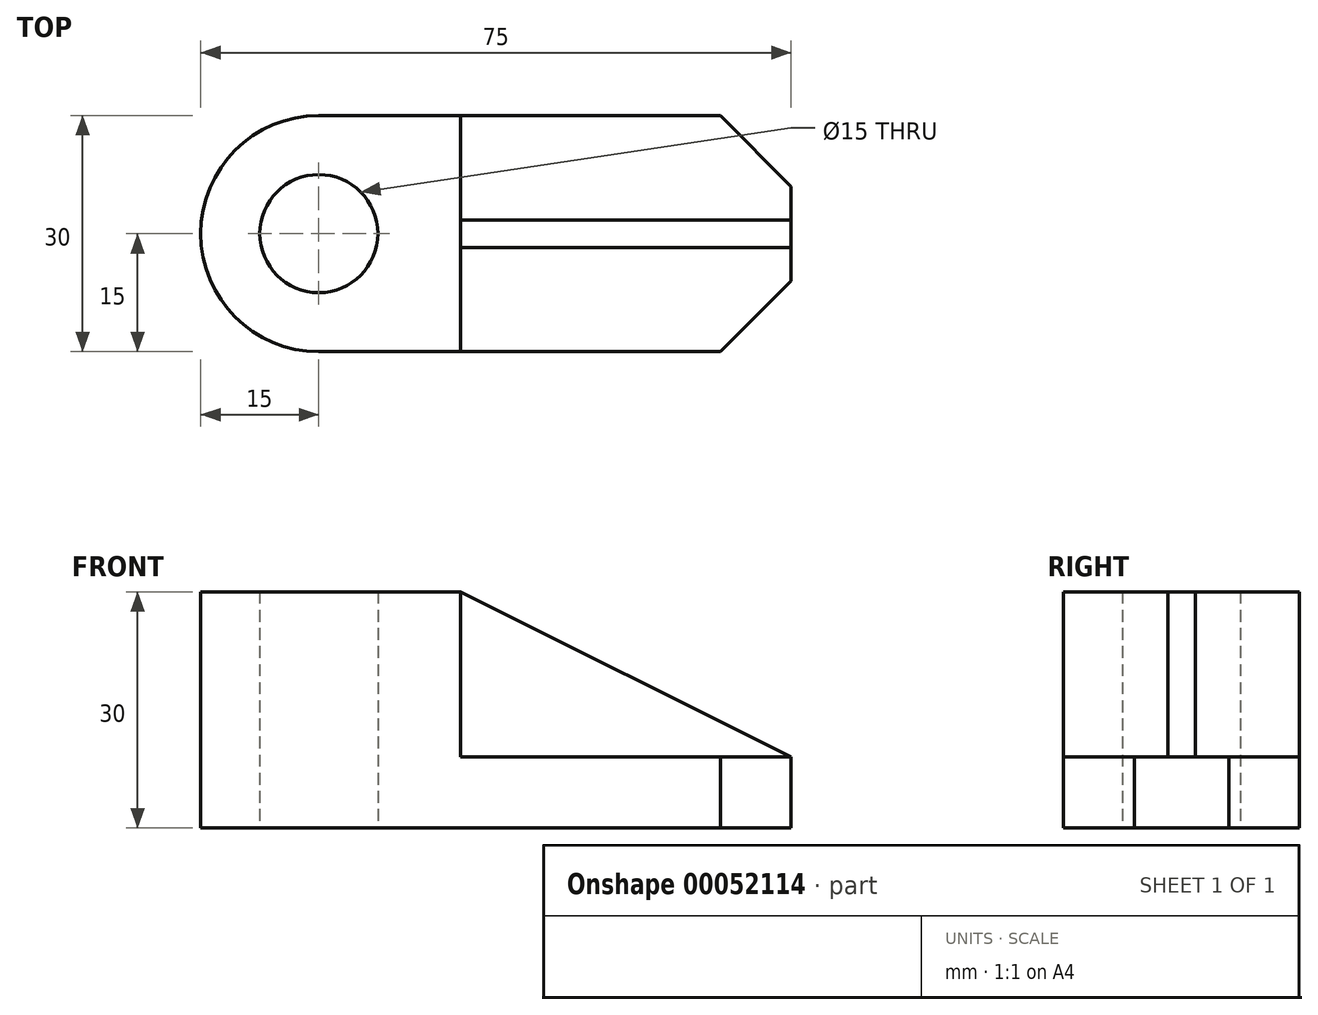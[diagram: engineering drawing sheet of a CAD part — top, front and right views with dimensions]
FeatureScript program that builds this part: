
annotation { "Feature Type Name" : "Feature", "Feature Type Description" : "" }
export const myFeature = defineFeature(function(context is Context, id is Id, definition is map)
    precondition{}
    {
        {
            var Q0;
            Q0=qCreatedBy(makeId("Top.planeOp"),FACE);
            var sketch = newSketch(context, id + "F0", { "sketchPlane" : qUnion([Q0])});
            skCircle(sketch, "E0", {"center": v(0, 0) * mm, "radius": 7.5 * mm});
            skArc(sketch, "E1", {"start": v(0, 15) * mm, "mid": v(-15, 0) * mm, "end": v(0, -15) * mm});
            skLineSegment(sketch, "E2", {"start": v(0, 15) * mm, "end": v(51, 15) * mm});
            skLineSegment(sketch, "E3", {"start": v(60, 6) * mm, "end": v(51, 15) * mm});
            skLineSegment(sketch, "E4.MirrorCS", {"start": v(0, -15) * mm, "end": v(51, -15) * mm});
            skLineSegment(sketch, "E5.MirrorCS", {"start": v(60, -6) * mm, "end": v(51, -15) * mm});
            skLineSegment(sketch, "E6", {"start": v(60, -6) * mm, "end": v(60, 6) * mm});
            skLineSegment(sketch, "E7", {"start": v(18, 15) * mm, "end": v(18, -15) * mm});
            skSolve(sketch);
        }
        {
            var Q0;
            Q0=makeQuery(id+"F0.imprint","IMPRINT",FACE,{"disambiguationData":[TD([[makeQuery(id+"F0.imprint","IMPRINT",EDGE,{"derivedFrom":sQuery(id+"F0.wireOp",EDGE,"E0")}),-1.0]])]});
            extrude(context, id + "F1", {"entities" : qUnion([Q0]), "depth" : 30 * mm});
        }
        {
            var Q0;
            Q0 = qSketchRegion(id + "F0", true);
            extrude(context, id + "F2", {"entities" : qUnion([Q0]), "operationType" : NewBodyOperationType.ADD, "depth" : 9 * mm});
        }
        {
            var Q0;
            Q0=qCreatedBy(makeId("Front.planeOp"),FACE);
            var sketch = newSketch(context, id + "F3", { "sketchPlane" : qUnion([Q0])});
            skLineSegment(sketch, "E8", {"start": v(0, 0) * mm, "end": v(0, 30) * mm, "construction": true});
            skLineSegment(sketch, "E9", {"start": v(0, 30) * mm, "end": v(18, 30) * mm, "construction": true});
            skLineSegment(sketch, "E10", {"start": v(0, 0) * mm, "end": v(0, 9) * mm, "construction": true});
            skLineSegment(sketch, "E11", {"start": v(0, 9) * mm, "end": v(18, 9) * mm, "construction": true});
            skLineSegment(sketch, "E12", {"start": v(18, 30) * mm, "end": v(60, 9) * mm});
            skLineSegment(sketch, "E13", {"start": v(18, 9) * mm, "end": v(18, 30) * mm});
            skLineSegment(sketch, "E14", {"start": v(18, 9) * mm, "end": v(60, 9) * mm});
            skSolve(sketch);
        }
        {
            var Q0;
            Q0=makeQuery(id+"F3.imprint","IMPRINT",FACE,{"disambiguationData":[TD([[makeQuery(id+"F3.imprint","IMPRINT",EDGE,{"derivedFrom":sQuery(id+"F3.wireOp",EDGE,"E12")}),-1.0]])]});
            extrude(context, id + "F4", {"entities" : qUnion([Q0]), "operationType" : NewBodyOperationType.ADD, "endBound" : BoundingType.SYMMETRIC, "depth" : 3.5 * mm});
        }
    });
